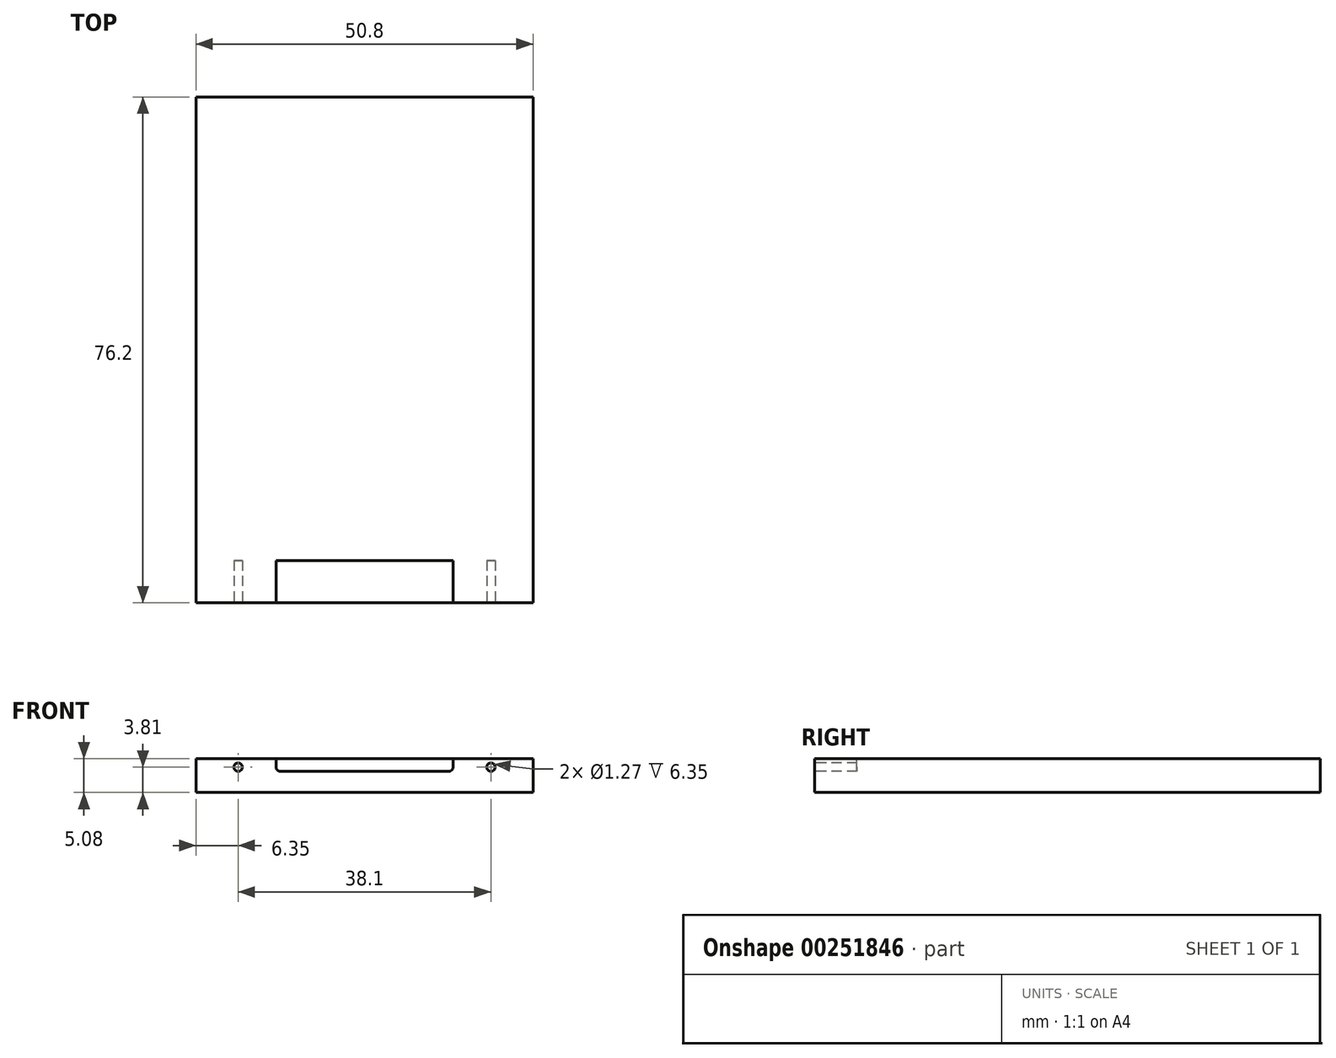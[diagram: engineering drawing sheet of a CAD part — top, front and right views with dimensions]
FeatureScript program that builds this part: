
annotation { "Feature Type Name" : "Feature", "Feature Type Description" : "" }
export const myFeature = defineFeature(function(context is Context, id is Id, definition is map)
    precondition{}
    {
        {
            var Q0;
            Q0=qCreatedBy(makeId("Front.planeOp"),FACE);
            var sketch = newSketch(context, id + "F0", { "sketchPlane" : qUnion([Q0])});
            skLineSegment(sketch, "E0.bottom", {"start": v(25.4, 2.54) * mm, "end": v(-25.4, 2.54) * mm});
            skLineSegment(sketch, "E0.top", {"start": v(25.4, -2.54) * mm, "end": v(-25.4, -2.54) * mm});
            skLineSegment(sketch, "E0.left", {"start": v(25.4, 2.54) * mm, "end": v(25.4, -2.54) * mm});
            skLineSegment(sketch, "E0.right", {"start": v(-25.4, 2.54) * mm, "end": v(-25.4, -2.54) * mm});
            skPoint(sketch, "E0.middle", {"position": v(0, 0) * mm});
            skSolve(sketch);
        }
        {
            var Q0;
            Q0 = qSketchRegion(id + "F0", true);
            extrude(context, id + "F1", {"entities" : qUnion([Q0]), "endBound" : BoundingType.SYMMETRIC, "depth" : 76.2 * mm});
        }
        {
            var Q0;
            Q0=makeQuery(id+"F1.opExtrude","CAP_FACE",FACE,{"disambiguationData":[OSD([sQuery(id+"F0.wireOp",EDGE,"E0.bottom"),sQuery(id+"F0.wireOp",EDGE,"E0.top"),sQuery(id+"F0.wireOp",EDGE,"E0.left"),sQuery(id+"F0.wireOp",EDGE,"E0.right")])],"isStart":false});
            var sketch = newSketch(context, id + "F2", { "sketchPlane" : qUnion([Q0])});
            skCircle(sketch, "E1", {"center": v(-19.05, 1.27) * mm, "radius": 0.64 * mm});
            skLineSegment(sketch, "E2", {"start": v(-12.7, 0.64) * mm, "end": v(0, 0.64) * mm});
            skLineSegment(sketch, "E3", {"start": v(-13.34, 1.27) * mm, "end": v(-13.34, 2.54) * mm});
            skArc(sketch, "E4", {"start": v(-13.34, 1.27) * mm, "mid": v(-13.15, 0.82) * mm, "end": v(-12.7, 0.64) * mm});
            skLineSegment(sketch, "E5.MirrorCS", {"start": v(12.7, 0.64) * mm, "end": v(0, 0.64) * mm});
            skArc(sketch, "E6.MirrorCS", {"start": v(13.34, 1.27) * mm, "mid": v(13.15, 0.82) * mm, "end": v(12.7, 0.64) * mm});
            skCircle(sketch, "E7.MirrorC", {"center": v(19.05, 1.27) * mm, "radius": 0.64 * mm});
            skLineSegment(sketch, "E8.MirrorCS", {"start": v(13.34, 1.27) * mm, "end": v(13.34, 2.54) * mm});
            skLineSegment(sketch, "E9", {"start": v(-13.34, 2.54) * mm, "end": v(13.34, 2.54) * mm});
            skSolve(sketch);
        }
        {
            var Q0;
            Q0 = qSketchRegion(id + "F2", true);
            extrude(context, id + "F3", {"entities" : qUnion([Q0]), "operationType" : NewBodyOperationType.REMOVE, "oppositeDirection" : true, "depth" : 6.35 * mm});
        }
    });
